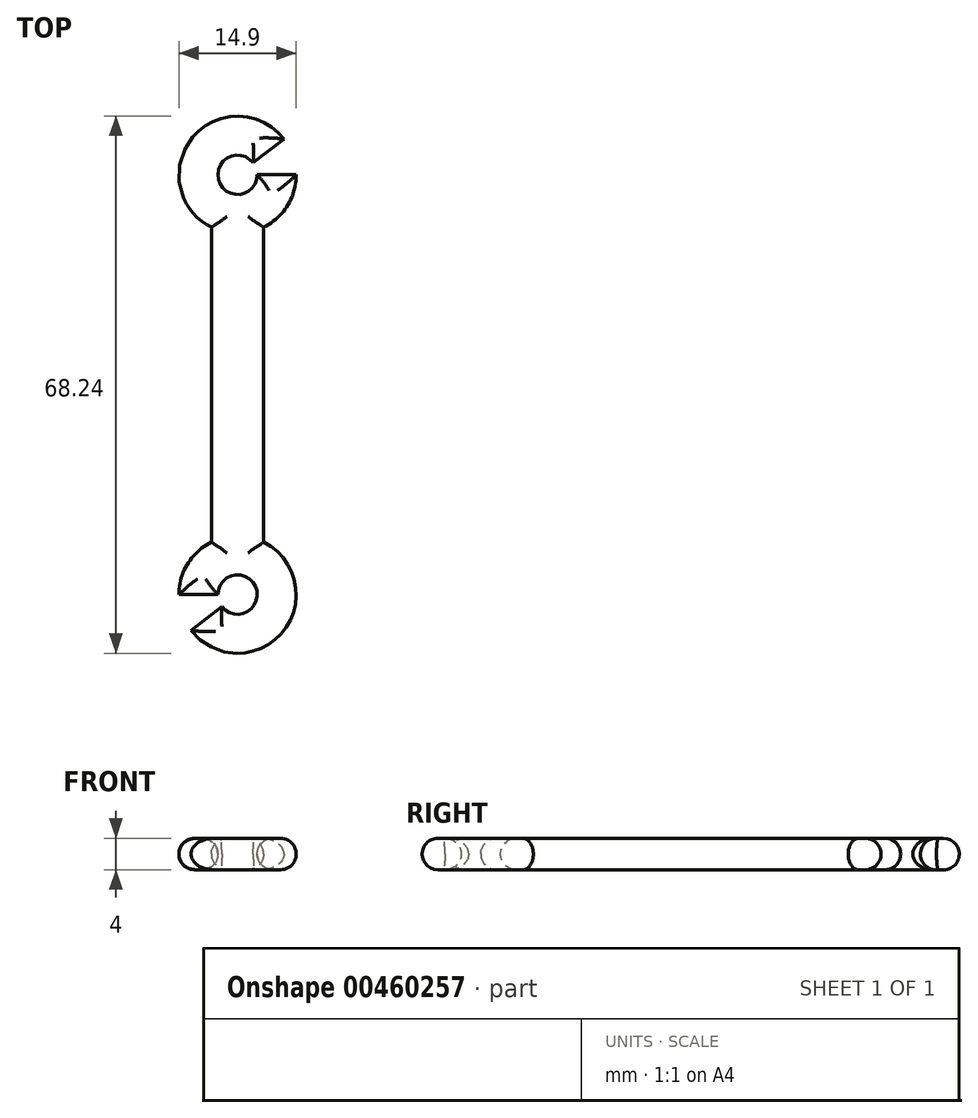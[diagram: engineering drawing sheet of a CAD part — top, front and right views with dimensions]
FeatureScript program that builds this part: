
annotation { "Feature Type Name" : "Feature", "Feature Type Description" : "" }
export const myFeature = defineFeature(function(context is Context, id is Id, definition is map)
    precondition{}
    {
        {
            var Q0;
            Q0=qCreatedBy(makeId("Top.planeOp"),FACE);
            var sketch = newSketch(context, id + "F0", { "sketchPlane" : qUnion([Q0])});
            skArc(sketch, "E0", {"start": v(3.33, 20) * mm, "mid": v(6.34, 22.75) * mm, "end": v(7.45, 26.67) * mm});
            skArc(sketch, "E1.MirrorC", {"start": v(3.33, -20) * mm, "mid": v(5.75, -31.4) * mm, "end": v(-5.9, -31.2) * mm});
            skLineSegment(sketch, "E2", {"start": v(3.33, 20) * mm, "end": v(3.33, -20) * mm});
            skLineSegment(sketch, "E3.MirrorCS", {"start": v(-3.33, 20) * mm, "end": v(-3.33, -20) * mm});
            skArc(sketch, "E4", {"start": v(1.98, 28.2) * mm, "mid": v(-2.37, 25.86) * mm, "end": v(2.5, 26.67) * mm});
            skArc(sketch, "E5", {"start": v(-1.98, -28.2) * mm, "mid": v(2.37, -25.86) * mm, "end": v(-2.5, -26.67) * mm});
            skLineSegment(sketch, "E6", {"start": v(2.5, 26.67) * mm, "end": v(7.45, 26.67) * mm});
            skLineSegment(sketch, "E7", {"start": v(1.98, 28.2) * mm, "end": v(5.9, 31.2) * mm});
            skLineSegment(sketch, "E8.MirrorCS", {"start": v(-2.5, -26.67) * mm, "end": v(-7.45, -26.67) * mm});
            skLineSegment(sketch, "E9.MirrorCS", {"start": v(-1.98, -28.2) * mm, "end": v(-5.9, -31.2) * mm});
            skPoint(sketch, "E10.orphan", {"position": v(7.45, -26.67) * mm});
            skArc(sketch, "E11.trimOffspring", {"start": v(5.9, 31.2) * mm, "mid": v(-5.75, 31.4) * mm, "end": v(-3.33, 20) * mm});
            skArc(sketch, "E12.trimOffspring", {"start": v(-7.45, -26.67) * mm, "mid": v(-6.34, -22.75) * mm, "end": v(-3.33, -20) * mm});
            skSolve(sketch);
        }
        {
            var Q0;
            Q0 = qSketchRegion(id + "F0", true);
            extrude(context, id + "F1", {"entities" : qUnion([Q0]), "depth" : 4 * mm});
        }
        {
            var Q0;
            Q0=makeQuery(id+"F1.opExtrude","CAP_FACE",FACE,{"disambiguationData":[OSD([sQuery(id+"F0.wireOp",EDGE,"E0"),sQuery(id+"F0.wireOp",EDGE,"E1.MirrorC"),sQuery(id+"F0.wireOp",EDGE,"E2"),sQuery(id+"F0.wireOp",EDGE,"E3.MirrorCS"),sQuery(id+"F0.wireOp",EDGE,"E4"),sQuery(id+"F0.wireOp",EDGE,"E5"),sQuery(id+"F0.wireOp",EDGE,"E6"),sQuery(id+"F0.wireOp",EDGE,"E7"),sQuery(id+"F0.wireOp",EDGE,"E8.MirrorCS"),sQuery(id+"F0.wireOp",EDGE,"E9.MirrorCS"),sQuery(id+"F0.wireOp",EDGE,"E11.trimOffspring"),sQuery(id+"F0.wireOp",EDGE,"E12.trimOffspring")])],"isStart":false});
            fillet(context, id + "F2", {"entities" : qUnion([Q0]), "radius" : 2 * mm, "tangentPropagation" : true, "allowEdgeOverflow" : false});
        }
        {
            var Q0;
            Q0=makeQuery(id+"F1.opExtrude","CAP_FACE",FACE,{"disambiguationData":[OSD([sQuery(id+"F0.wireOp",EDGE,"E0"),sQuery(id+"F0.wireOp",EDGE,"E1.MirrorC"),sQuery(id+"F0.wireOp",EDGE,"E2"),sQuery(id+"F0.wireOp",EDGE,"E3.MirrorCS"),sQuery(id+"F0.wireOp",EDGE,"E4"),sQuery(id+"F0.wireOp",EDGE,"E5"),sQuery(id+"F0.wireOp",EDGE,"E6"),sQuery(id+"F0.wireOp",EDGE,"E7"),sQuery(id+"F0.wireOp",EDGE,"E8.MirrorCS"),sQuery(id+"F0.wireOp",EDGE,"E9.MirrorCS"),sQuery(id+"F0.wireOp",EDGE,"E11.trimOffspring"),sQuery(id+"F0.wireOp",EDGE,"E12.trimOffspring")])],"isStart":true});
            fillet(context, id + "F3", {"entities" : qUnion([Q0]), "radius" : 2 * mm, "tangentPropagation" : true, "allowEdgeOverflow" : false});
        }
    });
